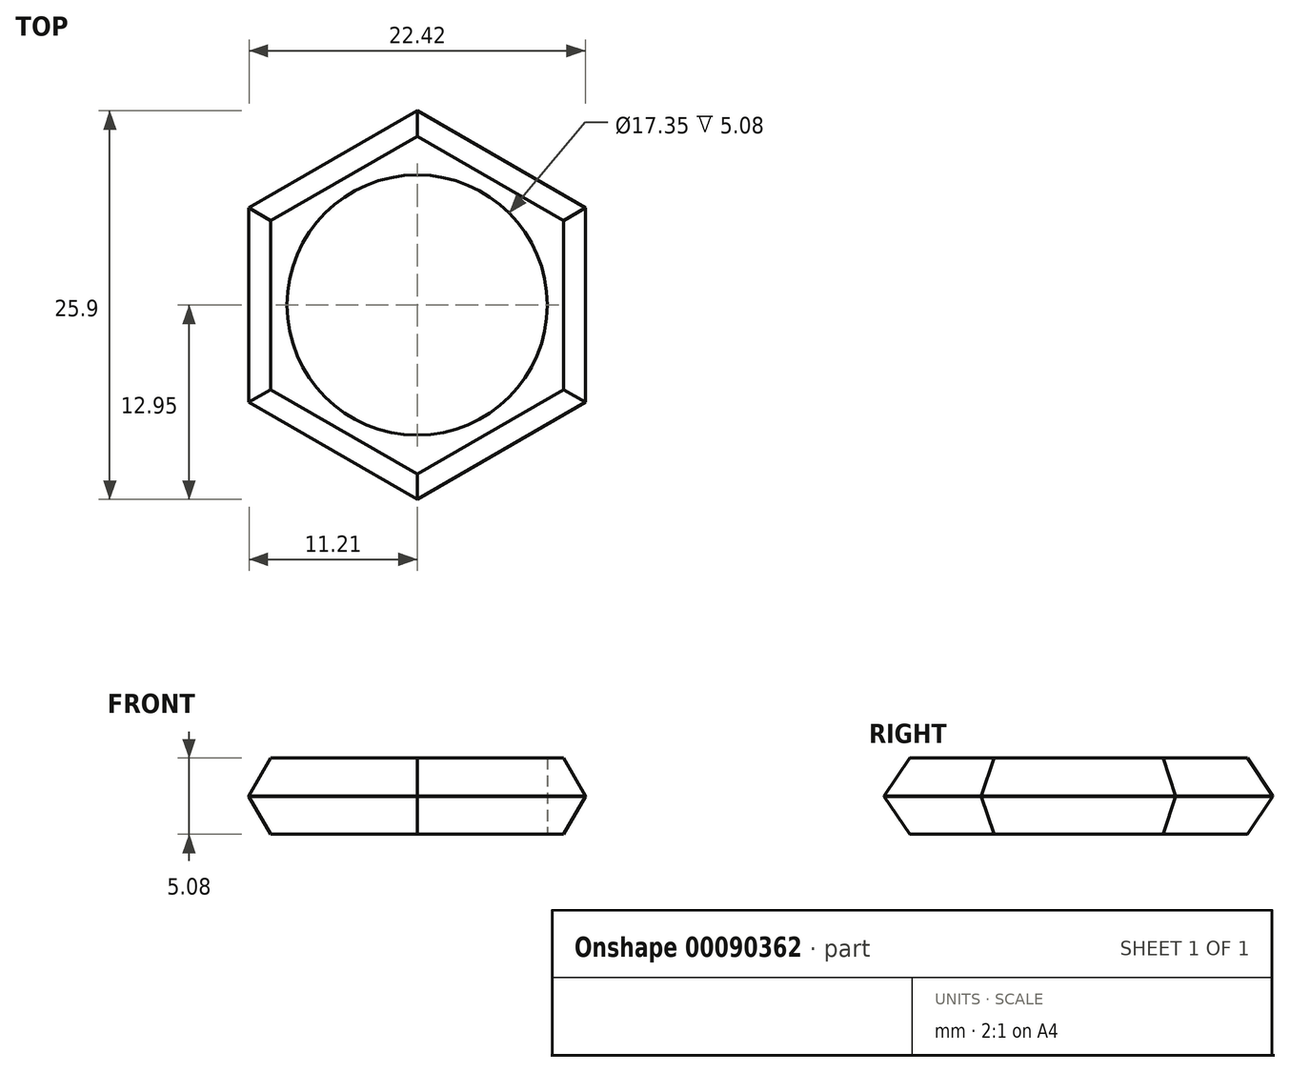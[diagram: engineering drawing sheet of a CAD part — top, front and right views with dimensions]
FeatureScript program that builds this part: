
annotation { "Feature Type Name" : "Feature", "Feature Type Description" : "" }
export const myFeature = defineFeature(function(context is Context, id is Id, definition is map)
    precondition{}
    {
        {
            var Q0;
            Q0=qCreatedBy(makeId("Top.planeOp"),FACE);
            var sketch = newSketch(context, id + "F0", { "sketchPlane" : qUnion([Q0])});
            skCircle(sketch, "E0", {"center": v(0, 0) * mm, "radius": 8.67 * mm});
            skCircle(sketch, "E1.cCircle", {"center": v(0, 0) * mm, "radius": 11.21 * mm, "construction": true});
            skLineSegment(sketch, "E1.0", {"start": v(11.21, 6.47) * mm, "end": v(11.21, -6.47) * mm});
            skLineSegment(sketch, "E1.1", {"start": v(11.21, -6.47) * mm, "end": v(0, -12.95) * mm});
            skLineSegment(sketch, "E1.2", {"start": v(0, -12.95) * mm, "end": v(-11.21, -6.47) * mm});
            skLineSegment(sketch, "E1.3", {"start": v(-11.21, -6.47) * mm, "end": v(-11.21, 6.47) * mm});
            skLineSegment(sketch, "E1.4", {"start": v(-11.21, 6.47) * mm, "end": v(0, 12.95) * mm});
            skLineSegment(sketch, "E1.5", {"start": v(0, 12.95) * mm, "end": v(11.21, 6.47) * mm});
            skPoint(sketch, "E1.0.midPoint", {"position": v(11.21, 0) * mm});
            skSolve(sketch);
        }
        {
            var Q0;
            Q0=makeQuery(id+"F0.imprint","IMPRINT",FACE,{"disambiguationData":[TD([[makeQuery(id+"F0.imprint","IMPRINT",EDGE,{"derivedFrom":sQuery(id+"F0.wireOp",EDGE,"E0")}),-1.0]])]});
            extrude(context, id + "F1", {"entities" : qUnion([Q0]), "depth" : 2.54 * mm, "hasSecondDirection" : true, "secondDirectionOppositeDirection" : true, "secondDirectionDepth" : 2.54 * mm});
        }
        {
            var Q0;
            Q0=makeQuery(id+"F1.opExtrude","CAP_EDGE",EDGE,{"disambiguationData":[OSD([sQuery(id+"F0.wireOp",EDGE,"E1.4")])],"isStart":false});
            var Q1;
            Q1=makeQuery(id+"F1.opExtrude","CAP_EDGE",EDGE,{"disambiguationData":[OSD([sQuery(id+"F0.wireOp",EDGE,"E1.3")])],"isStart":false});
            var Q2;
            Q2=makeQuery(id+"F1.opExtrude","CAP_EDGE",EDGE,{"disambiguationData":[OSD([sQuery(id+"F0.wireOp",EDGE,"E1.2")])],"isStart":false});
            var Q3;
            Q3=makeQuery(id+"F1.opExtrude","CAP_EDGE",EDGE,{"disambiguationData":[OSD([sQuery(id+"F0.wireOp",EDGE,"E1.1")])],"isStart":false});
            var Q4;
            Q4=makeQuery(id+"F1.opExtrude","CAP_EDGE",EDGE,{"disambiguationData":[OSD([sQuery(id+"F0.wireOp",EDGE,"E1.0")])],"isStart":false});
            var Q5;
            Q5=makeQuery(id+"F1.opExtrude","CAP_EDGE",EDGE,{"disambiguationData":[OSD([sQuery(id+"F0.wireOp",EDGE,"E1.5")])],"isStart":false});
            chamfer(context, id + "F2", {"entities" : qUnion([Q0, Q1, Q2, Q3, Q4, Q5]), "chamferType" : ChamferType.OFFSET_ANGLE, "width" : 1.46 * mm, "oppositeDirection" : true, "angle" : 60 * degree});
        }
        {
            var Q0;
            Q0=makeQuery(id+"F1.opExtrude","CAP_EDGE",EDGE,{"disambiguationData":[OSD([sQuery(id+"F0.wireOp",EDGE,"E1.4")])],"isStart":true});
            var Q1;
            Q1=makeQuery(id+"F1.opExtrude","CAP_EDGE",EDGE,{"disambiguationData":[OSD([sQuery(id+"F0.wireOp",EDGE,"E1.3")])],"isStart":true});
            var Q2;
            Q2=makeQuery(id+"F1.opExtrude","CAP_EDGE",EDGE,{"disambiguationData":[OSD([sQuery(id+"F0.wireOp",EDGE,"E1.2")])],"isStart":true});
            var Q3;
            Q3=makeQuery(id+"F1.opExtrude","CAP_EDGE",EDGE,{"disambiguationData":[OSD([sQuery(id+"F0.wireOp",EDGE,"E1.1")])],"isStart":true});
            var Q4;
            Q4=makeQuery(id+"F1.opExtrude","CAP_EDGE",EDGE,{"disambiguationData":[OSD([sQuery(id+"F0.wireOp",EDGE,"E1.0")])],"isStart":true});
            var Q5;
            Q5=makeQuery(id+"F1.opExtrude","CAP_EDGE",EDGE,{"disambiguationData":[OSD([sQuery(id+"F0.wireOp",EDGE,"E1.5")])],"isStart":true});
            chamfer(context, id + "F3", {"entities" : qUnion([Q0, Q1, Q2, Q3, Q4, Q5]), "chamferType" : ChamferType.OFFSET_ANGLE, "width" : 1.46 * mm, "oppositeDirection" : false, "angle" : 60 * degree, "tangentPropagation" : true});
        }
    });
